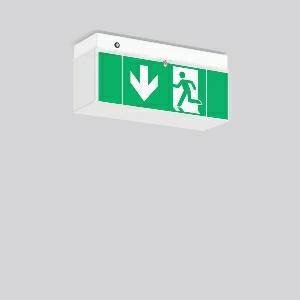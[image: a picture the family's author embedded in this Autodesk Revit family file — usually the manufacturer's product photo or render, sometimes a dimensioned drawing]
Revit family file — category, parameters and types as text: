
# Revit family: minisign_672189_002_fee1
name_source: partatom
category: Lighting Fixtures
units: mm (PartAtom-declared; Revit-internal decimal feet)

## family parameters
Cut with Voids When Loaded = No
Host = Face
Light Source = No
Part Type = Normal
Room Calculation Point = No
Round Connector Dimension = Use Diameter
Shared = No

## types (1)
- MINISIGN
    Apparent Load = 0 VA
    Default Elevation = 1800 mm
    Description = Series: MINISIGN
Luminaires for escape route identification Base: metal, powder-coated. Diffuser: plastic (polycarbonate), opal. 4 plastic foils with escape route motifs included (ISO 7010). Electronic ballast included. Self-contained system with automatic self-test. 
Colour: white
Length: 230 mm
Width: 103 mm
Height: 76 mm
Weight: 660 g
Operating mode: maintained power mode
Viewing Distance: 14 m
Duration time: 8 h
Lamp: LED
Socket: without socket
Colour temperature: 6500K
Colour rendering index (CRI): 70
System power: 4.8 W
System power, emergency: -
Control gear: EB
Protection class: I
Type of protection: IP 40
    Height = 76 mm
    Lamp = 0 x
    Length = 230 mm
    Luminous efficacy = 0 lm/W
    Manufacturer = RZB
    ModVariant = No
    Model = 672189.002
    Mounting Place = Ceiling, Wall
    Mounting Type = Surface mounted
    Number of Poles = 1
    OnlyDefault = Yes
    Power Factor = 1
    Product Name = MINISIGN
    Product group = Surface mounted ceiling and wall luminaires
    ProductGroupID = 305
    Protection Class = Protection class I
    Protection Degree = IP 40
    RLX_Detail_Level = 1
    RLX_Emergency_Light_Flux = 0 lm
    RLX_Emergency_Type = 0
    RLX_Emergency_Type_DB = No
    RlxData = <blob elided: 36121 chars, md5=a80fcc13>
    Standby Power = 0 W
    System Light Flux = 0 lm
    System Power = 0 W
    Type Comments = Product without accessories
    Type Image = 672188.002.jpg
    URL = http://relux.com
    VarID = ---
    Voltage = 230 V
    Voltage Range = 220-240 V
    Weight = 0.00 kg
    Width = 103 mm

## geometry (parser evidence)
native form markers: Blend x4, Sweep x10
no freeform markers — native parametric forms only
